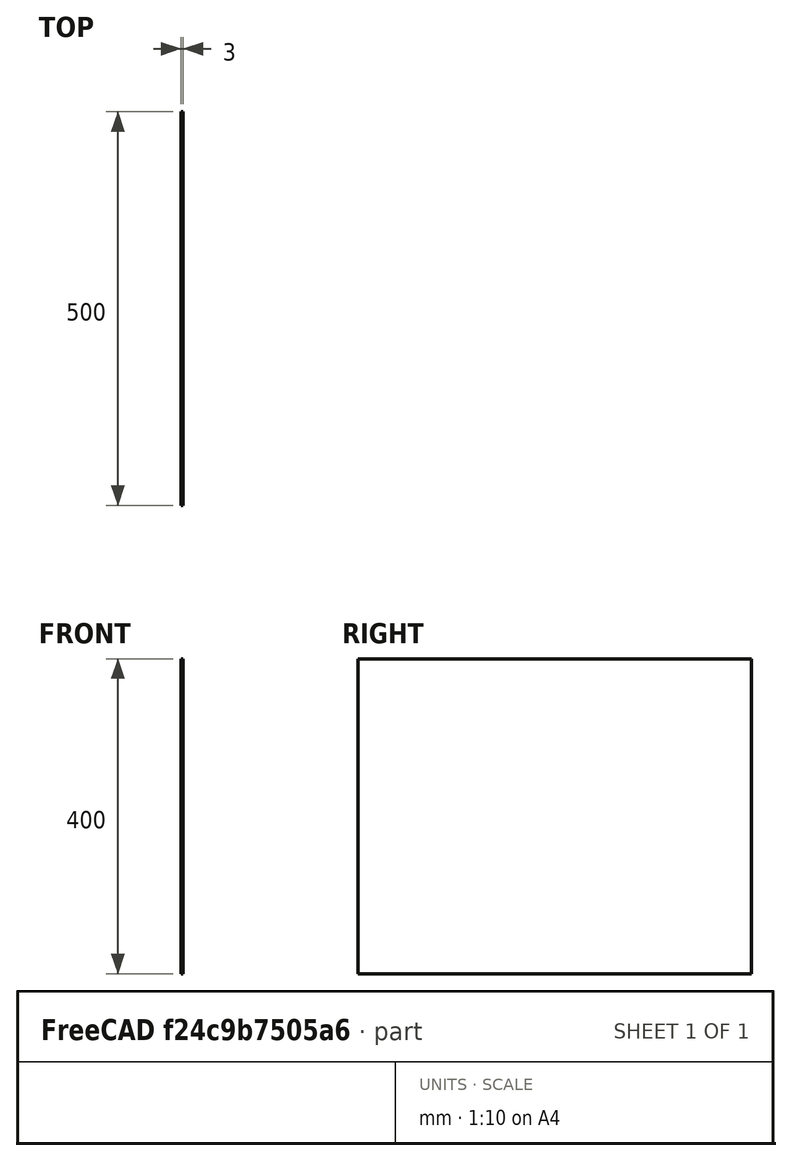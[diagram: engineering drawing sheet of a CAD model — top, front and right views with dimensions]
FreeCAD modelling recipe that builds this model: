
FCSTD DOCUMENT  (FreeCAD 0.18R16131 (Git))
Label: 4000_Body_Window_YZ
License: All rights reserved
LicenseURL: http://en.wikipedia.org/wiki/All_rights_reserved
objects: Sketcher::SketchObject×1, Spreadsheet::Sheet×1, PartDesign::Pad×1, PartDesign::Body×1
note: 4 computed .brp shape members not serialized (recipe doc carries the construction recipe); baked Part::Feature solids carry a one-line shape summary decoded from their .brp

FEATURE [Sketcher::SketchObject] Sketch
  MapMode = 4
  Placement = pos=(0,0,0) rot=(0.57735,0.57735,0.57735;2.0944rad)
  Support = -> [XY_Plane]
  expr: Constraints[6] = Spreadsheet.nY
  expr: Constraints[5] = Spreadsheet.nZ
  sketch-geometry (5):
    g0: LineSegment StartX=0 StartY=0 StartZ=0 EndX=0 EndY=400 EndZ=0
    g1: LineSegment StartX=500 StartY=0 StartZ=0 EndX=500 EndY=400 EndZ=0
    g2: LineSegment StartX=500 StartY=400 StartZ=0 EndX=0 EndY=400 EndZ=0
    g3: LineSegment StartX=250 StartY=0 StartZ=0 EndX=0 EndY=0 EndZ=0
    g4: LineSegment StartX=500 StartY=0 StartZ=0 EndX=250 EndY=0 EndZ=0
  constraints (14):
    c: Vertical(g0)
    c: Vertical(g1)
    c: Coincident(g2,g1)
    c: Coincident(g2,g0)
    c: Horizontal(g2)
    c: DistanceY(g1,g1) = 400
    c: DistanceX(g2,g2) = 500
    c: Coincident(g3,g0)
    c: Coincident(g4,g1)
    c: Horizontal(g4)
    c: Equal(g3,g4)
    c: Coincident(g4,g3)
    c: Horizontal(g3)
    c: Coincident(g0,g-1)
FEATURE [Spreadsheet::Sheet] Spreadsheet  label="xls"
  cells = B7=KEYBOARD FRONT; B8=Width; C8=nY; D8(nY)=500; B9=Height; C9=nZ; D9(nZ)=400; E9=F(T); B10=Thickness; C10=nT; D10(nT)=3
FEATURE [PartDesign::Pad] Pad
  Length = 3
  Length2 = 100
  Profile = -> Sketch
  Reversed = true
  Type = 0
  expr: Length = Spreadsheet.nT
FEATURE [PartDesign::Body] Body
  Group = -> [Sketch,Pad]
  Origin = -> Origin
  Tip = -> Pad
